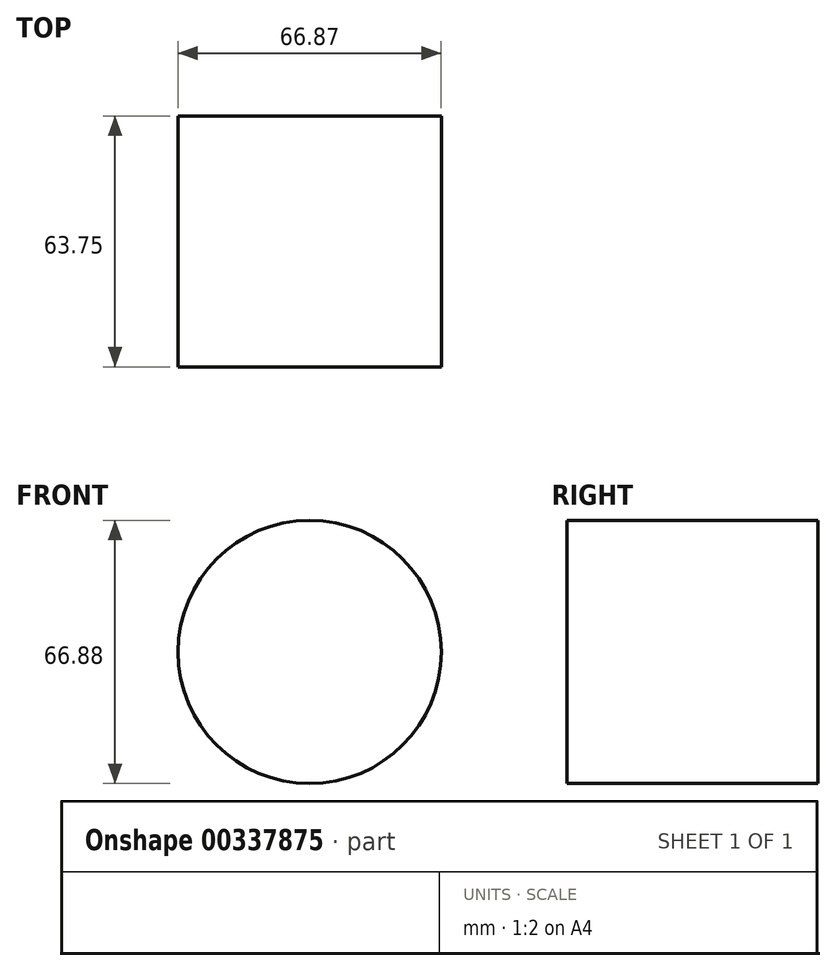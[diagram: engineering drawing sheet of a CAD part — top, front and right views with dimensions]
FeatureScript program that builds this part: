
annotation { "Feature Type Name" : "Feature", "Feature Type Description" : "" }
export const myFeature = defineFeature(function(context is Context, id is Id, definition is map)
    precondition{}
    {
        {
            var Q0;
            Q0=qCreatedBy(makeId("Front.planeOp"),FACE);
            var sketch = newSketch(context, id + "F0", { "sketchPlane" : qUnion([Q0])});
            skCircle(sketch, "E0", {"center": v(-49.68, 49.36) * mm, "radius": 33.44 * mm});
            skCircle(sketch, "E1", {"center": v(-49.68, 49.36) * mm, "radius": 40.42 * mm});
            skSolve(sketch);
        }
        {
            var Q0;
            Q0=makeQuery(id+"F0.imprint","IMPRINT",FACE,{"disambiguationData":[TD([[makeQuery(id+"F0.imprint","IMPRINT",EDGE,{"derivedFrom":sQuery(id+"F0.wireOp",EDGE,"E0")}),1.0]])]});
            extrude(context, id + "F1", {"entities" : qUnion([Q0]), "depth" : 63.75 * mm});
        }
    });
